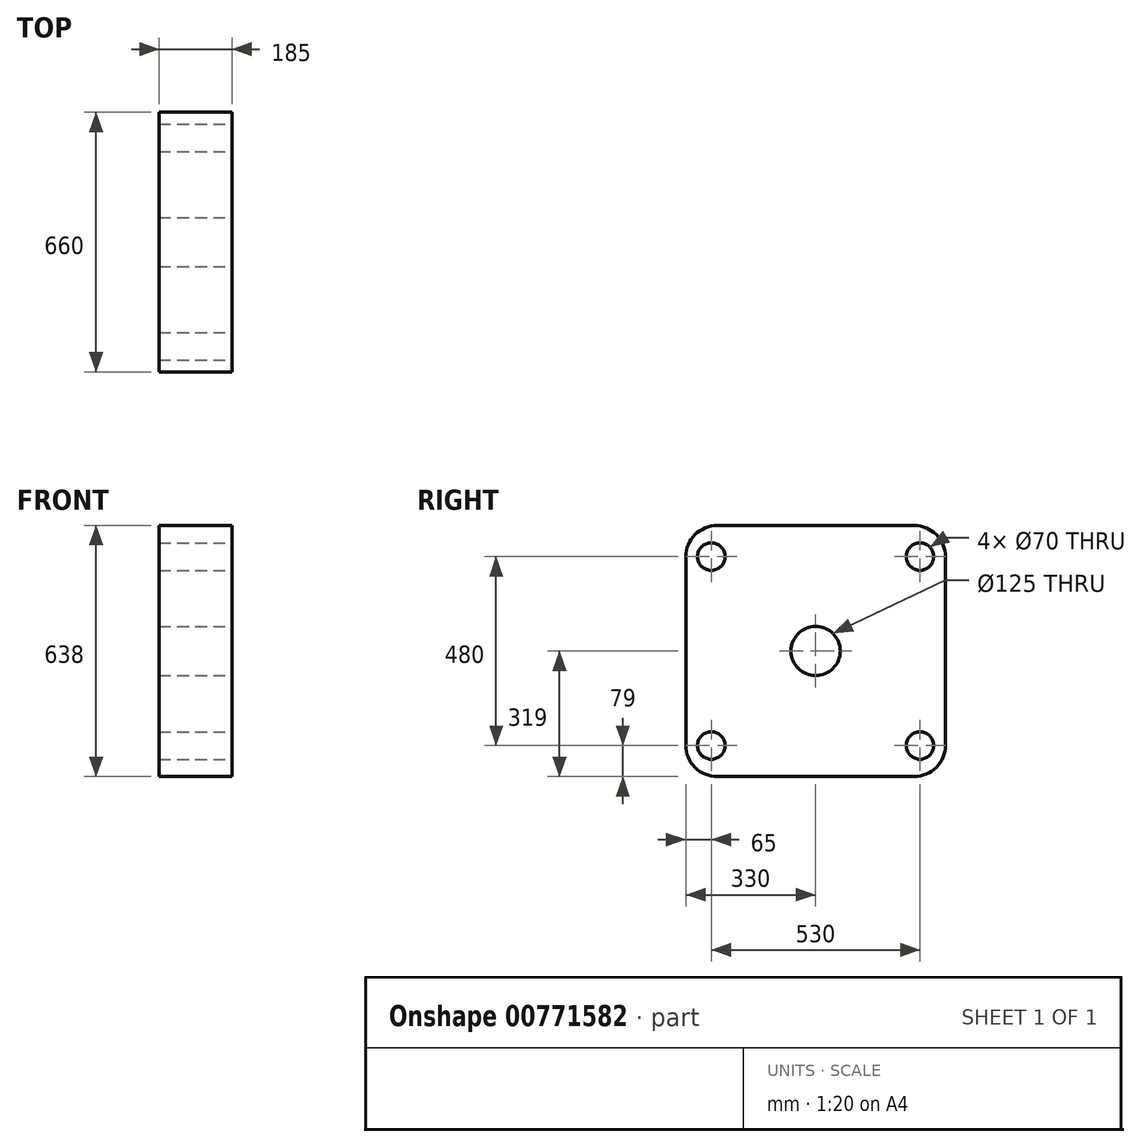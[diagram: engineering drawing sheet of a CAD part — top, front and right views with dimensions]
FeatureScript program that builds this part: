
annotation { "Feature Type Name" : "Feature", "Feature Type Description" : "" }
export const myFeature = defineFeature(function(context is Context, id is Id, definition is map)
    precondition{}
    {
        {
            var Q0;
            Q0=qCreatedBy(makeId("Right.planeOp"),FACE);
            var sketch = newSketch(context, id + "F0", { "sketchPlane" : qUnion([Q0])});
            skLineSegment(sketch, "E0.bottom", {"start": v(330, -319) * mm, "end": v(-330, -319) * mm});
            skLineSegment(sketch, "E0.top", {"start": v(330, 319) * mm, "end": v(-330, 319) * mm});
            skLineSegment(sketch, "E0.left", {"start": v(330, -319) * mm, "end": v(330, 319) * mm});
            skLineSegment(sketch, "E0.right", {"start": v(-330, -319) * mm, "end": v(-330, 319) * mm});
            skPoint(sketch, "E0.middle", {"position": v(0, 0) * mm});
            skSolve(sketch);
        }
        {
            var Q0;
            Q0=makeQuery(id+"F0.imprint","IMPRINT",FACE,{"disambiguationData":[TD([[makeQuery(id+"F0.imprint","IMPRINT",EDGE,{"derivedFrom":sQuery(id+"F0.wireOp",EDGE,"E0.bottom")}),-1.0]])]});
            extrude(context, id + "F1", {"entities" : qUnion([Q0]), "depth" : 185 * mm, "offsetDistance" : 25 * mm});
        }
        {
            var Q0;
            Q0=makeQuery(id+"F1.opExtrude","SWEPT_EDGE",EDGE,{"disambiguationData":[OSD([sQuery(id+"F0.wireOp",EDGE,"E0.top"),sQuery(id+"F0.wireOp",EDGE,"E0.left")])]});
            var Q1;
            Q1=makeQuery(id+"F1.opExtrude","SWEPT_EDGE",EDGE,{"disambiguationData":[OSD([sQuery(id+"F0.wireOp",EDGE,"E0.top"),sQuery(id+"F0.wireOp",EDGE,"E0.right")])]});
            var Q2;
            Q2=makeQuery(id+"F1.opExtrude","SWEPT_EDGE",EDGE,{"disambiguationData":[OSD([sQuery(id+"F0.wireOp",EDGE,"E0.bottom"),sQuery(id+"F0.wireOp",EDGE,"E0.left")])]});
            var Q3;
            Q3=makeQuery(id+"F1.opExtrude","SWEPT_EDGE",EDGE,{"disambiguationData":[OSD([sQuery(id+"F0.wireOp",EDGE,"E0.bottom"),sQuery(id+"F0.wireOp",EDGE,"E0.right")])]});
            fillet(context, id + "F2", {"entities" : qUnion([Q0, Q1, Q2, Q3]), "radius" : 80 * mm, "tangentPropagation" : true, "allowEdgeOverflow" : false});
        }
        {
            var Q0;
            Q0=makeQuery(id+"F1.opExtrude","CAP_FACE",FACE,{"disambiguationData":[OSD([sQuery(id+"F0.wireOp",EDGE,"E0.bottom"),sQuery(id+"F0.wireOp",EDGE,"E0.top"),sQuery(id+"F0.wireOp",EDGE,"E0.left"),sQuery(id+"F0.wireOp",EDGE,"E0.right")])],"isStart":false});
            var sketch = newSketch(context, id + "F3", { "sketchPlane" : qUnion([Q0])});
            skCircle(sketch, "E1", {"center": v(0, 0) * mm, "radius": 62.5 * mm});
            skSolve(sketch);
        }
        {
            var Q0;
            Q0=makeQuery(id+"F3.imprint","IMPRINT",FACE,{"disambiguationData":[TD([[makeQuery(id+"F3.imprint","IMPRINT",EDGE,{"derivedFrom":sQuery(id+"F3.wireOp",EDGE,"E1")}),1.0]])]});
            extrude(context, id + "F4", {"entities" : qUnion([Q0]), "operationType" : NewBodyOperationType.REMOVE, "endBound" : BoundingType.THROUGH_ALL, "oppositeDirection" : true, "depth" : 25 * mm, "offsetDistance" : 25 * mm});
        }
        {
            var Q0;
            Q0=makeQuery(id+"F1.opExtrude","CAP_FACE",FACE,{"disambiguationData":[OSD([sQuery(id+"F0.wireOp",EDGE,"E0.bottom"),sQuery(id+"F0.wireOp",EDGE,"E0.top"),sQuery(id+"F0.wireOp",EDGE,"E0.left"),sQuery(id+"F0.wireOp",EDGE,"E0.right")])],"isStart":false});
            var sketch = newSketch(context, id + "F5", { "sketchPlane" : qUnion([Q0])});
            skPoint(sketch, "E2", {"position": v(-265, 240) * mm});
            skPoint(sketch, "E3", {"position": v(265, 240) * mm});
            skPoint(sketch, "E4", {"position": v(265, -240) * mm});
            skPoint(sketch, "E5", {"position": v(-265, -240) * mm});
            skCircle(sketch, "E6", {"center": v(-265, 240) * mm, "radius": 35 * mm});
            skCircle(sketch, "E7", {"center": v(265, 240) * mm, "radius": 35 * mm});
            skCircle(sketch, "E8", {"center": v(265, -240) * mm, "radius": 35 * mm});
            skCircle(sketch, "E9", {"center": v(-265, -240) * mm, "radius": 35 * mm});
            skSolve(sketch);
        }
        {
            var Q0;
            Q0=makeQuery(id+"F5.imprint","IMPRINT",FACE,{"disambiguationData":[TD([[makeQuery(id+"F5.imprint","IMPRINT",EDGE,{"derivedFrom":sQuery(id+"F5.wireOp",EDGE,"E6")}),1.0]])]});
            var Q1;
            Q1=makeQuery(id+"F5.imprint","IMPRINT",FACE,{"disambiguationData":[TD([[makeQuery(id+"F5.imprint","IMPRINT",EDGE,{"derivedFrom":sQuery(id+"F5.wireOp",EDGE,"E7")}),1.0]])]});
            var Q2;
            Q2=makeQuery(id+"F5.imprint","IMPRINT",FACE,{"disambiguationData":[TD([[makeQuery(id+"F5.imprint","IMPRINT",EDGE,{"derivedFrom":sQuery(id+"F5.wireOp",EDGE,"E8")}),1.0]])]});
            var Q3;
            Q3=makeQuery(id+"F5.imprint","IMPRINT",FACE,{"disambiguationData":[TD([[makeQuery(id+"F5.imprint","IMPRINT",EDGE,{"derivedFrom":sQuery(id+"F5.wireOp",EDGE,"E9")}),1.0]])]});
            extrude(context, id + "F6", {"entities" : qUnion([Q0, Q1, Q2, Q3]), "operationType" : NewBodyOperationType.REMOVE, "endBound" : BoundingType.THROUGH_ALL, "oppositeDirection" : true, "depth" : 25 * mm, "offsetDistance" : 25 * mm});
        }
    });
